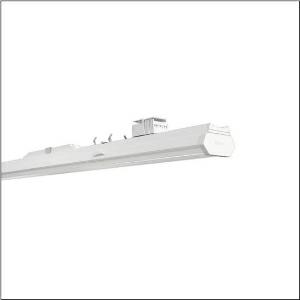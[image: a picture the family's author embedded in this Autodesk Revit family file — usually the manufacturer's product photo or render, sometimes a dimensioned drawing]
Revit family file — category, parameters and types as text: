
# Revit family: licross_21_protected_mo_52td1bvn455g
name_source: partatom
category: Lighting Fixtures
units: mm (PartAtom-declared; Revit-internal decimal feet)

## family parameters
Cut with Voids When Loaded = No
Host = Face
Light Source = No
Part Type = Normal
Room Calculation Point = No
Round Connector Dimension = Use Diameter
Shared = No

## types (1)
- --- (1 x LED, 5500 lm, 32.3 W, 4000K)
    Apparent Load = 32 VA
    CIE Flux Codes = 54 82 95 97 100
    Color Rendering = 80
    Color Temperature = 4000K
    Default Elevation = 1800 mm
    Description = Licross 21 Protected MO, luminaire insert, of sheet steel, galvanised, coil coated, white, length: 1.500mm, width: 90mm, height: 101mm, LED rated luminous flux: 5.500lm, light colour: 840, SDCM (Standard Deviation of Colour Matching)MacAdam ≤ 3 SDCM (initial), control gear: DALI 2, CLO, with plug, 5-pole, with phase selection, mains connection: 220..240V, AC, 50/60Hz, start of lifetime: 32W, end of service life: 38W, internal wiring halogen-free, primary optical cover: cover, of PMMA, light emission: direct distribution, primary light characteristic: symmetric, protection rating (complete): IP54, insulation class (complete): insulation class I (protective earthing), certification: CE, ENEC, VDE, UKCA, protection symbol: D if used in an environment with non-conductive dust loads with corresponding accessories, impact resistance: IK06, permissible ambient temperature for indoor applications: -25..+45°C, corresponds to IFS (International Featured Standards) requirements for safety and quality in the food industry, reducing of maximum allowable ambient temperature of 5°C with ceiling mounting, LABS conformity tested according to VDMA 24364:2018-05, The light source and the operating device comply with the requirements of the Ecodesign Regulation (EU) 2019/2020 and are replaceable in accordance with this regulation, packaging unit: 1 piece
    Height = 92 mm
    Lamp = 1 x LED
    Lamp Light Flux = 5500 lm
    Lamp Power = 32.3 W
    Lamp count = 1
    Length = 1500 mm
    Luminous efficacy = 170 lm/W
    Manufacturer = Siteco
    ModVariant = No
    Model = 52TD1BVN455G
    Mounting Place = Ceiling
    Mounting Type = Pendant
    Number of Poles = 1
    OnlyDefault = Yes
    Power Factor = 1
    Product Name = Licross 21 Protected MO
    Product group = luminaire insert | ceiling pendant
    ProductGroupID = 901
    Protection Class = Protection class I
    Protection Degree = IP 54
    RLX_Detail_Level = 1
    RLX_Emergency_Light_Flux = 0 lm
    RLX_Emergency_Type = 0
    RLX_Emergency_Type_DB = No
    RlxData = <blob elided: 24341 chars, md5=f571de24>
    Socket = socket
    Standby Power = 0 W
    System Light Flux = 5500 lm
    System Power = 32 W
    Type Comments = factory setting: luminous flux: 100 % | dim-lin: 254 | 219 mA
    Type Image = l_1256148.jpg
    URL = http://relux.com
    VarID = @adj_087829
    Voltage = 0 V
    Weight = 0.00 kg
    Width = 88 mm

## geometry (parser evidence)
native form markers: Blend x4, Sweep x11
no freeform markers — native parametric forms only
